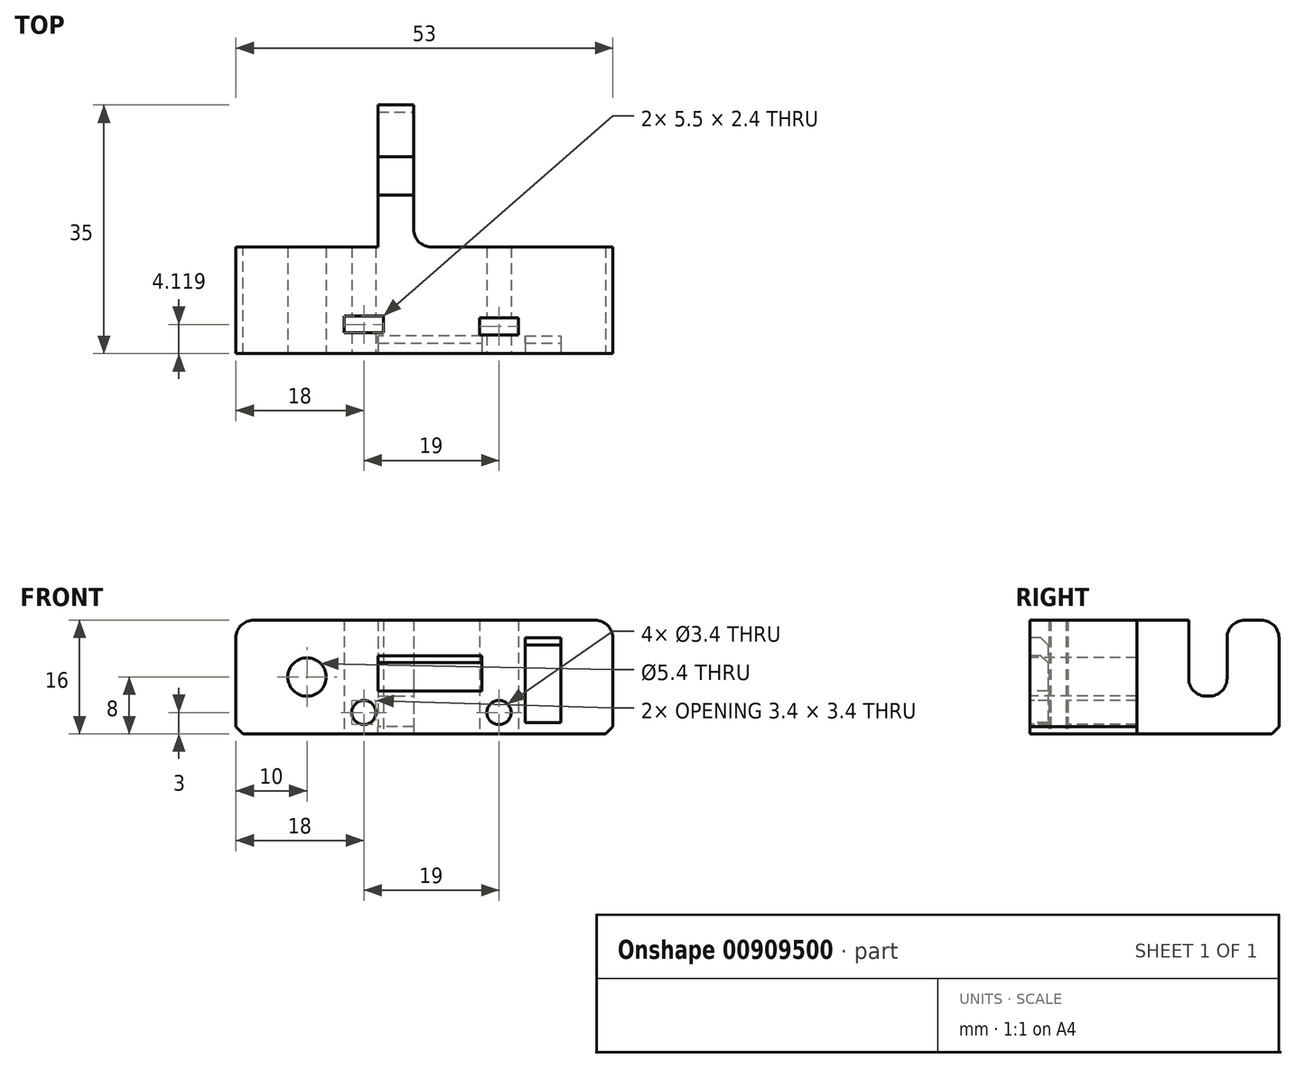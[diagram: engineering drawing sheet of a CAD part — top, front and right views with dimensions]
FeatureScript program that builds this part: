
annotation { "Feature Type Name" : "Feature", "Feature Type Description" : "" }
export const myFeature = defineFeature(function(context is Context, id is Id, definition is map)
    precondition{}
    {
        {
            var Q0;
            Q0=qCreatedBy(makeId("Top.planeOp"),FACE);
            var sketch = newSketch(context, id + "F0", { "sketchPlane" : qUnion([Q0])});
            skLineSegment(sketch, "E0", {"start": v(0, 20) * mm, "end": v(0, 0) * mm});
            skLineSegment(sketch, "E1", {"start": v(0, 0) * mm, "end": v(-20, 0) * mm});
            skLineSegment(sketch, "E2", {"start": v(-20, 0) * mm, "end": v(-20, -15) * mm});
            skLineSegment(sketch, "E3", {"start": v(-20, -15) * mm, "end": v(33, -15) * mm});
            skLineSegment(sketch, "E4", {"start": v(33, -15) * mm, "end": v(33, 0) * mm});
            skLineSegment(sketch, "E5", {"start": v(33, 0) * mm, "end": v(5, 0) * mm});
            skLineSegment(sketch, "E6", {"start": v(5, 0) * mm, "end": v(5, 20) * mm});
            skLineSegment(sketch, "E7", {"start": v(5, 20) * mm, "end": v(0, 20) * mm});
            skSolve(sketch);
        }
        {
            var Q0;
            Q0=makeQuery(id+"F0.imprint","IMPRINT",FACE,{"disambiguationData":[TD([[makeQuery(id+"F0.imprint","IMPRINT",EDGE,{"derivedFrom":sQuery(id+"F0.wireOp",EDGE,"E0")}),1.0]])]});
            extrude(context, id + "F1", {"entities" : qUnion([Q0]), "depth" : 16 * mm, "offsetDistance" : 25 * mm});
        }
        {
            var Q0;
            Q0=makeQuery(id+"F1.opExtrude","SWEPT_FACE",FACE,{"disambiguationData":[OSD([sQuery(id+"F0.wireOp",EDGE,"E3")])]});
            var sketch = newSketch(context, id + "F2", { "sketchPlane" : qUnion([Q0])});
            skCircle(sketch, "E8", {"center": v(-2, 3) * mm, "radius": 1.7 * mm});
            skCircle(sketch, "E9", {"center": v(17, 3) * mm, "radius": 1.7 * mm});
            skLineSegment(sketch, "E10", {"start": v(14.61, 6) * mm, "end": v(0, 6) * mm});
            skLineSegment(sketch, "E11", {"start": v(0, 6) * mm, "end": v(0, 11) * mm});
            skLineSegment(sketch, "E12", {"start": v(0, 11) * mm, "end": v(14.61, 11) * mm});
            skLineSegment(sketch, "E13", {"start": v(14.61, 11) * mm, "end": v(14.61, 6) * mm});
            skLineSegment(sketch, "E14.bottom", {"start": v(20.7, 13.5) * mm, "end": v(25.7, 13.5) * mm});
            skLineSegment(sketch, "E14.top", {"start": v(20.7, 1.58) * mm, "end": v(25.7, 1.58) * mm});
            skLineSegment(sketch, "E14.left", {"start": v(20.7, 13.5) * mm, "end": v(20.7, 1.58) * mm});
            skLineSegment(sketch, "E14.right", {"start": v(25.7, 13.5) * mm, "end": v(25.7, 1.58) * mm});
            skCircle(sketch, "E15", {"center": v(-10, 8) * mm, "radius": 2.7 * mm});
            skSolve(sketch);
        }
        {
            var Q0;
            Q0=makeQuery(id+"F2.imprint","IMPRINT",FACE,{"disambiguationData":[TD([[makeQuery(id+"F2.imprint","IMPRINT",EDGE,{"derivedFrom":sQuery(id+"F2.wireOp",EDGE,"E9")}),1.0]])]});
            var Q1;
            Q1=makeQuery(id+"F2.imprint","IMPRINT",FACE,{"disambiguationData":[TD([[makeQuery(id+"F2.imprint","IMPRINT",EDGE,{"derivedFrom":sQuery(id+"F2.wireOp",EDGE,"E8")}),1.0]])]});
            extrude(context, id + "F3", {"entities" : qUnion([Q0, Q1]), "operationType" : NewBodyOperationType.REMOVE, "oppositeDirection" : true, "depth" : 25 * mm, "offsetDistance" : 25 * mm});
        }
        {
            var Q0;
            Q0=makeQuery(id+"F1.opExtrude","CAP_FACE",FACE,{"disambiguationData":[OSD([sQuery(id+"F0.wireOp",EDGE,"E0"),sQuery(id+"F0.wireOp",EDGE,"E1"),sQuery(id+"F0.wireOp",EDGE,"E2"),sQuery(id+"F0.wireOp",EDGE,"E3"),sQuery(id+"F0.wireOp",EDGE,"E4"),sQuery(id+"F0.wireOp",EDGE,"E5"),sQuery(id+"F0.wireOp",EDGE,"E6"),sQuery(id+"F0.wireOp",EDGE,"E7")])],"isStart":true});
            var sketch = newSketch(context, id + "F4", { "sketchPlane" : qUnion([Q0])});
            skLineSegment(sketch, "E16", {"start": v(-2, 18.38) * mm, "end": v(-2, -1.93) * mm, "construction": true});
            skLineSegment(sketch, "E17", {"start": v(17, 17.78) * mm, "end": v(17, -3.12) * mm, "construction": true});
            skLineSegment(sketch, "E18", {"start": v(-2, 12.08) * mm, "end": v(-4.75, 12.08) * mm});
            skLineSegment(sketch, "E19", {"start": v(-4.75, 12.08) * mm, "end": v(-4.75, 9.68) * mm});
            skLineSegment(sketch, "E20", {"start": v(-4.75, 9.68) * mm, "end": v(-2, 9.68) * mm});
            skLineSegment(sketch, "E21.MirrorCS", {"start": v(-2, 12.08) * mm, "end": v(0.75, 12.08) * mm});
            skLineSegment(sketch, "E22.MirrorCS", {"start": v(0.75, 12.08) * mm, "end": v(0.75, 9.68) * mm});
            skLineSegment(sketch, "E23.MirrorCS", {"start": v(0.75, 9.68) * mm, "end": v(-2, 9.68) * mm});
            skLineSegment(sketch, "E24", {"start": v(17, 12.35) * mm, "end": v(14.25, 12.35) * mm});
            skLineSegment(sketch, "E25", {"start": v(14.25, 12.35) * mm, "end": v(14.25, 9.95) * mm});
            skLineSegment(sketch, "E26", {"start": v(14.25, 9.95) * mm, "end": v(17, 9.95) * mm});
            skLineSegment(sketch, "E27.MirrorCS", {"start": v(17, 12.35) * mm, "end": v(19.75, 12.35) * mm});
            skLineSegment(sketch, "E28.MirrorCS", {"start": v(19.75, 12.35) * mm, "end": v(19.75, 9.95) * mm});
            skLineSegment(sketch, "E29.MirrorCS", {"start": v(19.75, 9.95) * mm, "end": v(17, 9.95) * mm});
            skSolve(sketch);
        }
        {
            var Q0;
            Q0=makeQuery(id+"F4.imprint","IMPRINT",FACE,{"disambiguationData":[TD([[makeQuery(id+"F4.imprint","IMPRINT",EDGE,{"derivedFrom":sQuery(id+"F4.wireOp",EDGE,"E24")}),1.0]])]});
            var Q1;
            Q1=makeQuery(id+"F4.imprint","IMPRINT",FACE,{"disambiguationData":[TD([[makeQuery(id+"F4.imprint","IMPRINT",EDGE,{"derivedFrom":sQuery(id+"F4.wireOp",EDGE,"E18")}),1.0]])]});
            extrude(context, id + "F5", {"entities" : qUnion([Q0, Q1]), "operationType" : NewBodyOperationType.REMOVE, "oppositeDirection" : true, "depth" : 25 * mm, "offsetDistance" : 25 * mm});
        }
        {
            var Q0;
            Q0=makeQuery(id+"F2.imprint","IMPRINT",FACE,{"disambiguationData":[TD([[makeQuery(id+"F2.imprint","IMPRINT",EDGE,{"derivedFrom":sQuery(id+"F2.wireOp",EDGE,"E10")}),-1.0]])]});
            var Q1;
            Q1=makeQuery(id+"F2.imprint","IMPRINT",FACE,{"disambiguationData":[TD([[makeQuery(id+"F2.imprint","IMPRINT",EDGE,{"derivedFrom":sQuery(id+"F2.wireOp",EDGE,"E14.bottom")}),-1.0]])]});
            extrude(context, id + "F6", {"entities" : qUnion([Q0, Q1]), "operationType" : NewBodyOperationType.REMOVE, "oppositeDirection" : true, "depth" : 2.5 * mm, "offsetDistance" : 25 * mm});
        }
        {
            var Q0;
            Q0=makeQuery(id+"F1.opExtrude","SWEPT_FACE",FACE,{"disambiguationData":[OSD([sQuery(id+"F0.wireOp",EDGE,"E6")])]});
            var sketch = newSketch(context, id + "F7", { "sketchPlane" : qUnion([Q0])});
            skLineSegment(sketch, "E30.bottom", {"start": v(7.3, 16) * mm, "end": v(12.7, 16) * mm});
            skLineSegment(sketch, "E30.top", {"start": v(7.3, 5.3) * mm, "end": v(12.7, 5.3) * mm});
            skLineSegment(sketch, "E30.left", {"start": v(7.3, 16) * mm, "end": v(7.3, 5.3) * mm});
            skLineSegment(sketch, "E30.right", {"start": v(12.7, 16) * mm, "end": v(12.7, 5.3) * mm});
            skSolve(sketch);
        }
        {
            var Q0;
            Q0=makeQuery(id+"F7.imprint","IMPRINT",FACE,{"disambiguationData":[TD([[makeQuery(id+"F7.imprint","IMPRINT",EDGE,{"derivedFrom":sQuery(id+"F7.wireOp",EDGE,"E30.bottom")}),-1.0]])]});
            extrude(context, id + "F8", {"entities" : qUnion([Q0]), "operationType" : NewBodyOperationType.REMOVE, "oppositeDirection" : true, "depth" : 25 * mm, "offsetDistance" : 25 * mm});
        }
        {
            var Q0;
            Q0=makeQuery(id+"F8.boolean.opBoolean","COPY",EDGE,{"derivedFrom":makeQuery(id+"F8.opExtrude","SWEPT_EDGE",EDGE,{"disambiguationData":[OSD([sQuery(id+"F7.wireOp",EDGE,"E30.top"),sQuery(id+"F7.wireOp",EDGE,"E30.left")])]})});
            var Q1;
            Q1=makeQuery(id+"F8.boolean.opBoolean","COPY",EDGE,{"derivedFrom":makeQuery(id+"F8.opExtrude","SWEPT_EDGE",EDGE,{"disambiguationData":[OSD([sQuery(id+"F7.wireOp",EDGE,"E30.top"),sQuery(id+"F7.wireOp",EDGE,"E30.right")])]})});
            var Q2;
            Q2=makeQuery(id+"F1.opExtrude","CAP_EDGE",EDGE,{"disambiguationData":[OSD([sQuery(id+"F0.wireOp",EDGE,"E7")])],"isStart":false});
            var Q3;
            Q3=makeQuery(id+"F1.opExtrude","CAP_EDGE",EDGE,{"disambiguationData":[OSD([sQuery(id+"F0.wireOp",EDGE,"E2")])],"isStart":false});
            var Q4;
            Q4=makeQuery(id+"F1.opExtrude","CAP_EDGE",EDGE,{"disambiguationData":[OSD([sQuery(id+"F0.wireOp",EDGE,"E4")])],"isStart":false});
            var Q5;
            Q5=makeQuery(id+"F8.boolean.opBoolean","COPY",EDGE,{"derivedFrom":makeQuery(id+"F8.opExtrude","SWEPT_EDGE",EDGE,{"disambiguationData":[OSD([sQuery(id+"F0.wireOp",EDGE,"E6"),sQuery(id+"F7.wireOp",EDGE,"E30.bottom"),sQuery(id+"F7.wireOp",EDGE,"E30.right")])]})});
            var Q6;
            Q6=makeQuery(id+"F8.boolean.opBoolean","COPY",EDGE,{"derivedFrom":makeQuery(id+"F8.opExtrude","SWEPT_EDGE",EDGE,{"disambiguationData":[OSD([sQuery(id+"F0.wireOp",EDGE,"E6"),sQuery(id+"F7.wireOp",EDGE,"E30.bottom"),sQuery(id+"F7.wireOp",EDGE,"E30.left")])]})});
            var Q7;
            Q7=makeQuery(id+"F1.opExtrude","SWEPT_EDGE",EDGE,{"disambiguationData":[OSD([sQuery(id+"F0.wireOp",EDGE,"E5"),sQuery(id+"F0.wireOp",EDGE,"E6")])]});
            fillet(context, id + "F9", {"entities" : qUnion([Q0, Q1, Q2, Q3, Q4, Q5, Q6, Q7]), "radius" : 2.5 * mm, "tangentPropagation" : true, "allowEdgeOverflow" : false});
        }
        {
            var Q0;
            Q0=makeQuery(id+"F6.boolean.opBoolean","COPY",EDGE,{"derivedFrom":makeQuery(id+"F6.opExtrude","CAP_EDGE",EDGE,{"disambiguationData":[OSD([sQuery(id+"F2.wireOp",EDGE,"E12")])],"isStart":false})});
            var Q1;
            Q1=makeQuery(id+"F6.boolean.opBoolean","COPY",EDGE,{"derivedFrom":makeQuery(id+"F6.opExtrude","CAP_EDGE",EDGE,{"disambiguationData":[OSD([sQuery(id+"F2.wireOp",EDGE,"E14.bottom")])],"isStart":false})});
            var Q2;
            Q2=makeQuery(id+"F1.opExtrude","CAP_EDGE",EDGE,{"disambiguationData":[OSD([sQuery(id+"F0.wireOp",EDGE,"E4")])],"isStart":true});
            var Q3;
            Q3=makeQuery(id+"F1.opExtrude","CAP_EDGE",EDGE,{"disambiguationData":[OSD([sQuery(id+"F0.wireOp",EDGE,"E2")])],"isStart":true});
            var Q4;
            Q4=makeQuery(id+"F1.opExtrude","CAP_EDGE",EDGE,{"disambiguationData":[OSD([sQuery(id+"F0.wireOp",EDGE,"E7")])],"isStart":true});
            chamfer(context, id + "F10", {"entities" : qUnion([Q0, Q1, Q2, Q3, Q4]), "width" : 1 * mm, "tangentPropagation" : true});
        }
        {
            var Q0;
            Q0=makeQuery(id+"F2.imprint","IMPRINT",FACE,{"disambiguationData":[TD([[makeQuery(id+"F2.imprint","IMPRINT",EDGE,{"derivedFrom":sQuery(id+"F2.wireOp",EDGE,"E15")}),1.0]])]});
            extrude(context, id + "F11", {"entities" : qUnion([Q0]), "operationType" : NewBodyOperationType.REMOVE, "oppositeDirection" : true, "depth" : 25 * mm, "offsetDistance" : 25 * mm});
        }
    });
